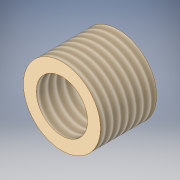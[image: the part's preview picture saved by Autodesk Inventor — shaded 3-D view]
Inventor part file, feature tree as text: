
AUTODESK INVENTOR PART (.ipt)
format: ipt  version: 2019.1 (Build 231200000, 200)  size: 116,736 bytes
history: native  units: in
note: dims shown in document units (in); Inventor stores cm internally (conversion verified against a paired STEP export)
features: thread x2, extrude x1, sketch x1
ambient origin geometry x8: Origin, YZ Plane, XZ Plane, XY Plane, X Axis, Y Axis, Z Axis, Center Point
bodies: Solid1 (feature_tree)
feature tree (4):
  extrude  "Extrusion1"  Depth=0.41in
  thread  "Thread1"  [1 undecoded]
  thread  "Thread2"  [1 undecoded]
  sketch  "Sketch1"  dims[d0=0.5625in d1=0.375in d2=0.41in d3=0.0in d4=1.0in d5=0.0in d6=1.0in d7=0.0in]
note: 2 required parameter values undecoded (feature->parameter linkage not recoverable at this tier; creation-order binding heuristic only, values carry confidence <= 0.55)
